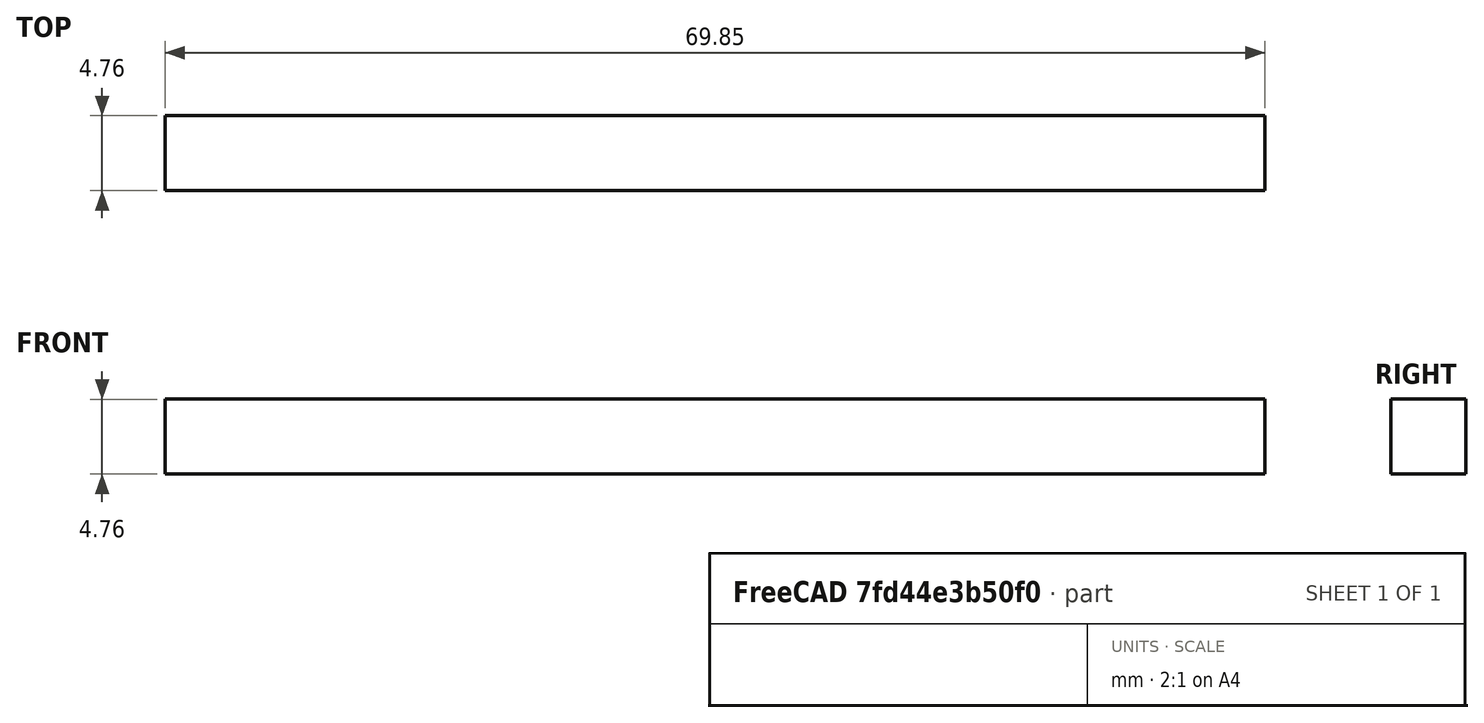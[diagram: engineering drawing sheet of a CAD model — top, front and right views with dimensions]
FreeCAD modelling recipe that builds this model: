
FCSTD DOCUMENT  (FreeCAD 2022.1128R26244 +5318 (Git))
Label: BYC33
License: All rights reserved
LicenseURL: http://en.wikipedia.org/wiki/All_rights_reserved
objects: Sketcher::SketchObject×1, PartDesign::Pad×1, PartDesign::Body×1
note: 6 computed .brp shape members not serialized (recipe doc carries the construction recipe); baked Part::Feature solids carry a one-line shape summary decoded from their .brp

FEATURE [Sketcher::SketchObject] Sketch
  ArcFitTolerance = 1e-06
  AttachmentSupport = -> [XY_Plane]
  ExternalBSplineMaxDegree = 5
  ExternalBSplineTolerance = 0.0001
  FullyConstrained = true
  InternalTolerance = 1e-06
  MakeInternals = false
  MapMode = 5
  Support = -> [XY_Plane]
  TreeRank = 10
  sketch-geometry (4):
    g0: LineSegment StartX=0 StartY=1e-16 StartZ=0 EndX=69.85 EndY=1e-16 EndZ=0
    g1: LineSegment StartX=69.85 StartY=1e-16 StartZ=0 EndX=69.85 EndY=4.7625 EndZ=0
    g2: LineSegment StartX=69.85 StartY=4.7625 StartZ=0 EndX=0 EndY=4.7625 EndZ=0
    g3: LineSegment StartX=0 StartY=4.7625 StartZ=0 EndX=0 EndY=0 EndZ=0
  constraints (11):
    c: Coincident(g0,g1)
    c: Coincident(g1,g2)
    c: Coincident(g2,g3)
    c: Coincident(g3,g0)
    c: Horizontal(g0)
    c: Horizontal(g2)
    c: Vertical(g1)
    c: Vertical(g3)
    c: DistanceX(g0,g0) = 69.85
    c: DistanceY(g3,g3) = 4.7625
    c: Coincident(g0,g-1)
FEATURE [PartDesign::Pad] Pad
  AddSubType = 0
  AlongSketchNormal = false
  AutoTaperInnerAngle = true
  CheckUpToFaceLimits = true
  ClaimChildren = false
  Direction = (0,0,1)
  Fit = 0
  FitJoin = 0
  InnerFit = 0
  InnerFitJoin = 0
  Length = 4.7625
  Length2 = 100
  Linearize = true
  NewSolid = false
  Profile = -> Sketch
  Refine = true
  Suppress = false
  TaperInnerAngle = 0
  TaperInnerAngleRev = 0
  TreeRank = 11
  Type = 0
  _ProfileBasedVersion = 1
FEATURE [PartDesign::Body] Body  label="BYC33"
  AutoGroupSolids = false
  ClaimAllChildren = false
  ExportMode = 0
  Group = -> [Sketch,Pad]
  Origin = -> Origin
  Tip = -> Pad
  TreeRank = 9
  _ExportChildren = -> [Pad]
  _GroupVersion = 1
